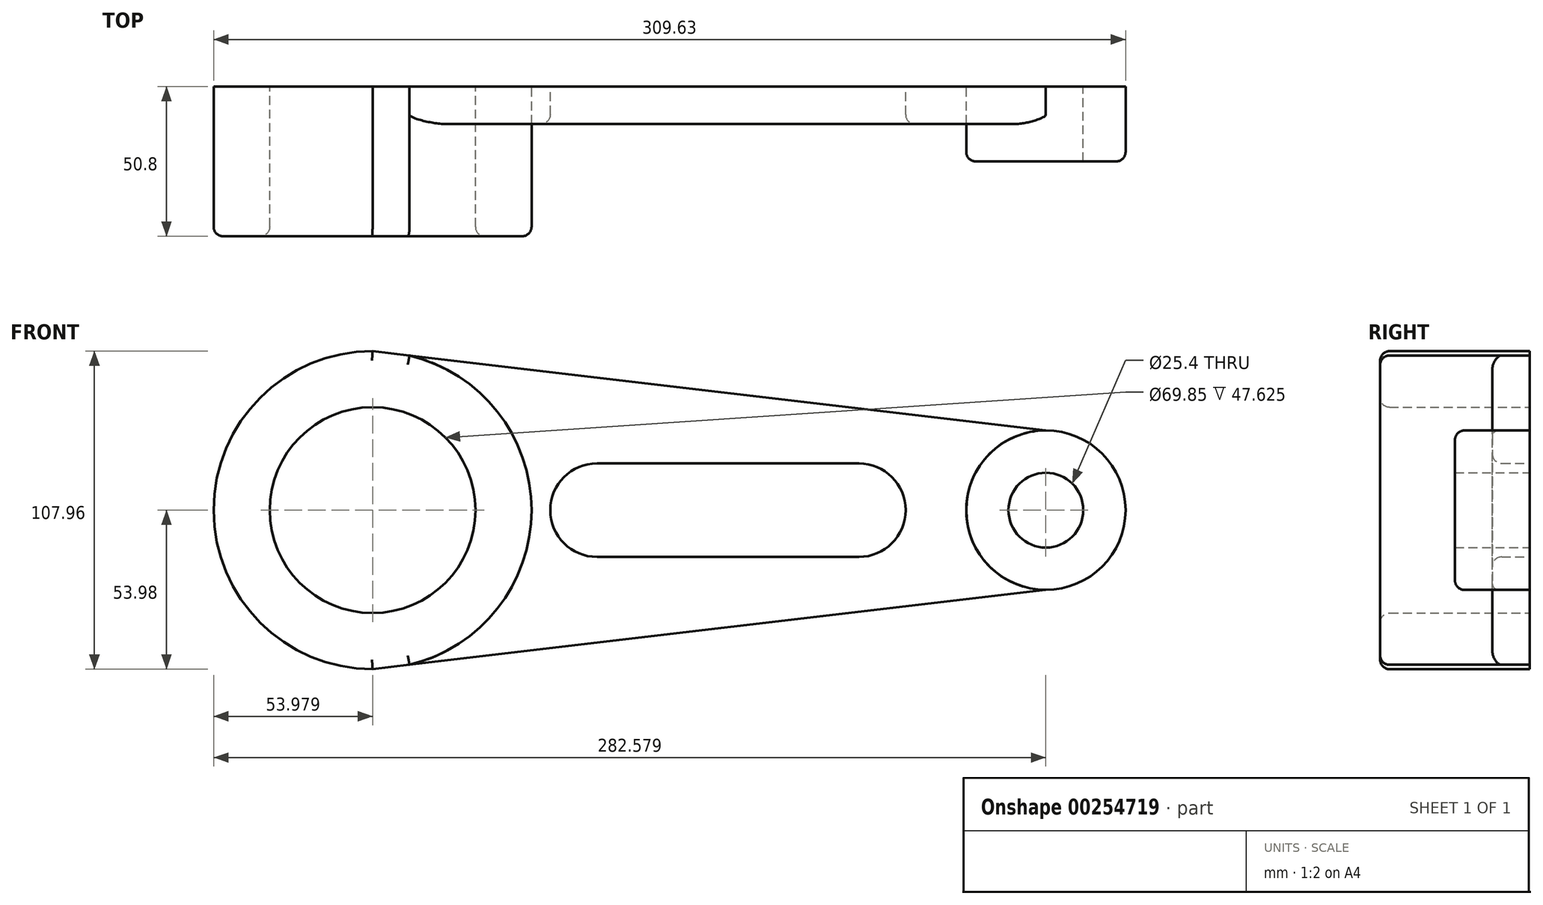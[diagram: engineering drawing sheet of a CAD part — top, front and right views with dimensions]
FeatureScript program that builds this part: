
annotation { "Feature Type Name" : "Feature", "Feature Type Description" : "" }
export const myFeature = defineFeature(function(context is Context, id is Id, definition is map)
    precondition{}
    {
        {
            var Q0;
            Q0=qCreatedBy(makeId("Front.planeOp"),FACE);
            var sketch = newSketch(context, id + "F0", { "sketchPlane" : qUnion([Q0])});
            skCircle(sketch, "E0", {"center": v(-154.6, 0) * mm, "radius": 53.98 * mm});
            skCircle(sketch, "E1", {"center": v(-154.6, 0) * mm, "radius": 34.93 * mm});
            skCircle(sketch, "E2", {"center": v(74, 0) * mm, "radius": 12.7 * mm});
            skCircle(sketch, "E3", {"center": v(74, 0) * mm, "radius": 27.05 * mm});
            skPoint(sketch, "E4", {"position": v(-78.4, 0) * mm});
            skPoint(sketch, "E5", {"position": v(10.5, 0) * mm});
            skArc(sketch, "E6", {"start": v(-78.4, 15.88) * mm, "mid": v(-94.28, 0) * mm, "end": v(-78.4, -15.88) * mm});
            skArc(sketch, "E7", {"start": v(10.5, -15.88) * mm, "mid": v(26.37, 0) * mm, "end": v(10.5, 15.88) * mm});
            skLineSegment(sketch, "E8", {"start": v(-78.4, 15.88) * mm, "end": v(10.5, 15.88) * mm});
            skLineSegment(sketch, "E9", {"start": v(-78.4, -15.88) * mm, "end": v(10.5, -15.88) * mm});
            skLineSegment(sketch, "E10", {"start": v(-154.6, 53.98) * mm, "end": v(74, 27.05) * mm});
            skLineSegment(sketch, "E11", {"start": v(-154.6, -53.98) * mm, "end": v(74, -27.05) * mm});
            skSolve(sketch);
        }
        {
            var Q0;
            Q0=makeQuery(id+"F0.imprint","IMPRINT",FACE,{"disambiguationData":[TD([[makeQuery(id+"F0.imprint","IMPRINT",EDGE,{"derivedFrom":sQuery(id+"F0.wireOp",EDGE,"E1")}),-1.0]])]});
            extrude(context, id + "F1", {"entities" : qUnion([Q0]), "depth" : 50.8 * mm});
        }
        {
            var Q0;
            Q0=makeQuery(id+"F0.imprint","IMPRINT",FACE,{"disambiguationData":[TD([[makeQuery(id+"F0.imprint","IMPRINT",EDGE,{"derivedFrom":sQuery(id+"F0.wireOp",EDGE,"E2")}),-1.0]])]});
            extrude(context, id + "F2", {"entities" : qUnion([Q0]), "depth" : 25.4 * mm});
        }
        {
            var Q0;
            Q0=makeQuery(id+"F0.imprint","IMPRINT",FACE,{"disambiguationData":[TD([[makeQuery(id+"F0.imprint","IMPRINT",EDGE,{"derivedFrom":sQuery(id+"F0.wireOp",EDGE,"E6")}),-1.0]])]});
            extrude(context, id + "F3", {"entities" : qUnion([Q0]), "depth" : 12.7 * mm, "offsetDistance" : 25.4 * mm});
        }
        {
            var Q0;
            Q0=makeQuery(id+"F1.opExtrude","CAP_FACE",FACE,{"disambiguationData":[OSD([sQuery(id+"F0.wireOp",EDGE,"E0"),sQuery(id+"F0.wireOp",EDGE,"E1"),sQuery(id+"F0.wireOp",EDGE,"E10"),sQuery(id+"F0.wireOp",EDGE,"E11")])],"isStart":false});
            var Q1;
            Q1=makeQuery(id+"F3.opExtrude","CAP_EDGE",EDGE,{"disambiguationData":[OSD([sQuery(id+"F0.wireOp",EDGE,"E10")])],"isStart":false});
            var Q2;
            Q2=makeQuery(id+"F3.opExtrude","CAP_EDGE",EDGE,{"disambiguationData":[OSD([sQuery(id+"F0.wireOp",EDGE,"E11")])],"isStart":false});
            var Q3;
            Q3=makeQuery(id+"F2.opExtrude","CAP_EDGE",EDGE,{"disambiguationData":[OSD([sQuery(id+"F0.wireOp",EDGE,"E3")])],"isStart":false});
            var Q4;
            Q4=makeQuery(id+"F3.opExtrude","CAP_EDGE",EDGE,{"disambiguationData":[OSD([sQuery(id+"F0.wireOp",EDGE,"E7")])],"isStart":false});
            fillet(context, id + "F4", {"entities" : qUnion([Q0, Q1, Q2, Q3, Q4]), "radius" : 3.17 * mm, "tangentPropagation" : true, "allowEdgeOverflow" : false});
        }
    });
